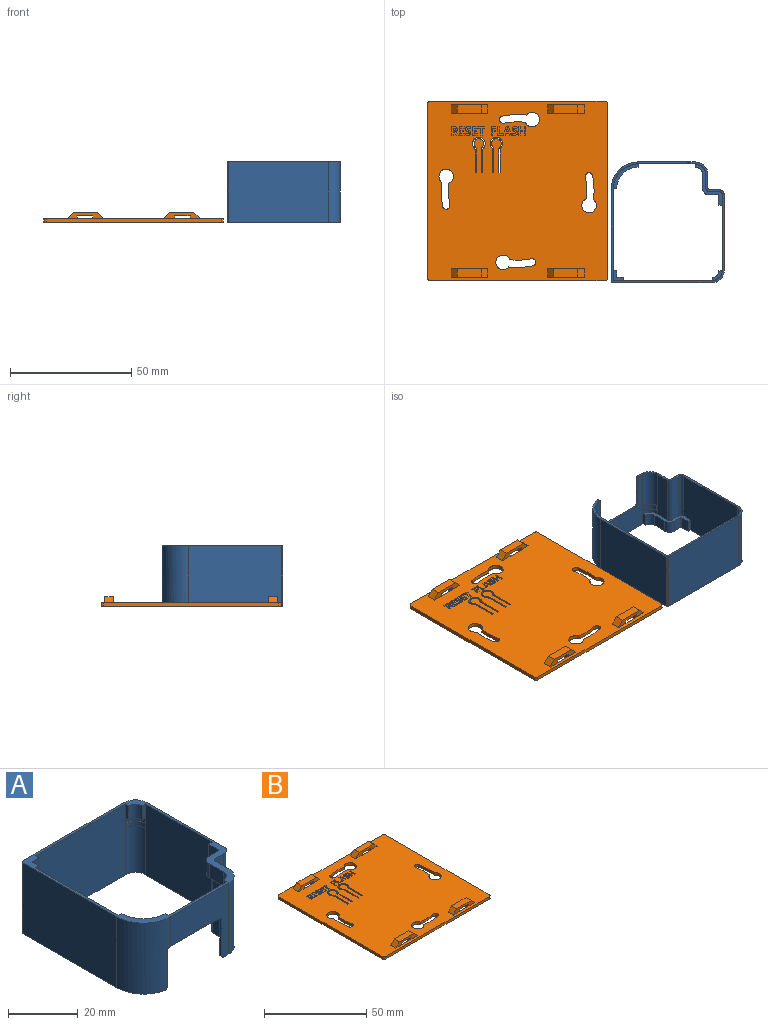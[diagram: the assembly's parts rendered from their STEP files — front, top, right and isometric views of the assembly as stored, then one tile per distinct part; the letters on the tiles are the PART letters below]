
ASSEMBLY  parts=2 mates=1
PART A: 74 faces, bbox 46.5x49.8x25 mm
  f0: plane 49.75x46.5mm, normal (0,0,1), area 215.3mm2, adj f38,f39,f40,f41,f42,f43,f44,f45
  f1: plane 2.42x0.2mm, normal (0,1,0), area 0.5mm2, adj f2,f3,f4,f11
  f2: cone r=2.6mm half-angle=60deg, axis (0,0,-1), area 1.5mm2, adj f1,f3,f19,f20
  f3: cylinder r=4mm len=4mm, axis (0,0,1), area 14.5mm2, adj f1,f2,f4,f20
  f4: plane 4.2x4.2mm, normal (0,0,1), area 1.3mm2, adj f1,f3,f20,f21
  f5: cone r=8.6mm half-angle=60deg, axis (0,0,-1), area 3.7mm2, adj f6,f22,f27,f28
  f6: cylinder r=10mm len=10mm, axis (0,0,1), area 36.3mm2, adj f5,f7,f22,f28
  f7: plane 10.2x10.2mm, normal (0,0,1), area 3.2mm2, adj f6,f22,f28,f29
  f8: cylinder r=4mm len=4mm, axis (0,0,1), area 9.3mm2, adj f9,f10,f18,f30
  f9: cone r=3.2mm half-angle=30deg, axis (0,0,-1), area 2.6mm2, adj f8,f18,f30,f31
  f10: plane 4.2x4.2mm, normal (0,0,1), area 1.3mm2, adj f8,f18,f30,f33
  f11: plane 20x5.8mm, normal (-1,0,0), area 116mm2, adj f1,f12,f19,f21,f37,f61
  f12: cylinder r=1.3mm len=20mm, axis (0,0,1), area 40.8mm2, adj f11,f13,f37,f61
  f13: plane 20x3.75mm, normal (0,1,0), area 75mm2, adj f12,f17,f37,f61
  f14: cylinder r=1mm len=1mm, axis (0,1,0), area 1.3mm2, adj f15,f23,f27,f73
  f15: plane 12.5x0.81mm, normal (1,0,0), area 10.1mm2, adj f14,f16,f27,f73
  f16: cylinder r=1mm len=1mm, axis (0,-1,0), area 1.3mm2, adj f15,f27,f61,f73
  f17: cylinder r=1.7mm len=20mm, axis (0,0,1), area 53.4mm2, adj f13,f37,f60,f61
  f18: plane 1.83x0.2mm, normal (0,-1,0), area 0.3mm2, adj f8,f9,f10,f60
  f19: cylinder r=4.2mm len=15.78mm, axis (0,0,1), area 104.1mm2, adj f2,f11,f52,f61
  f20: plane 2.42x0.2mm, normal (-1,0,0), area 0.5mm2, adj f2,f3,f4,f52
  f21: cylinder r=4.2mm len=4.2mm, axis (0,0,1), area 11.9mm2, adj f4,f11,f37,f52
  f22: plane 2.42x0.2mm, normal (1,0,0), area 0.5mm2, adj f5,f6,f7,f52
  f23: plane 20x0.8mm, normal (0,0,-1), area 16mm2, adj f14,f24,f27,f52,f72,f73
  f24: cylinder r=1mm len=1mm, axis (0,-1,0), area 1.3mm2, adj f23,f25,f52,f72
  f25: plane 12.5x0.8mm, normal (-1,0,0), area 10mm2, adj f24,f26,f52,f72
  f26: cylinder r=1mm len=1mm, axis (0,1,0), area 1.3mm2, adj f25,f52,f61,f72
  f27: cylinder r=10.2mm len=15.78mm, axis (0,0,1), area 234.6mm2, adj f5,f14,f15,f16,f23,f49,f52,f61
  f28: plane 2.42x0.2mm, normal (0,1,0), area 0.5mm2, adj f5,f6,f7,f49
  f29: cylinder r=10.2mm len=10.2mm, axis (0,0,1), area 28.8mm2, adj f7,f34,f49,f52
  f30: plane 1.83x0.2mm, normal (-1,0,0), area 0.3mm2, adj f8,f9,f10,f45
  f31: cylinder r=4.2mm len=16.37mm, axis (0,0,1), area 108mm2, adj f9,f45,f60,f61
  f32: cylinder r=0.5mm len=20mm, axis (0,0,1), area 15.7mm2, adj f36,f45,f49,f61
  f33: cylinder r=4.2mm len=4.2mm, axis (0,0,1), area 11.9mm2, adj f10,f35,f45,f60
  f34: plane 10.2x10.2mm, normal (0,0,-1), area 20.9mm2, adj f29,f39,f50,f51
  f35: plane 4.2x4.2mm, normal (0,0,-1), area 7.7mm2, adj f33,f42,f43,f44
  f36: plane 4.2x4.2mm, normal (0,0,-1), area 9.8mm2, adj f32,f40,f41,f45,f46,f47,f48,f49
  f37: plane 17x10.95mm, normal (0,0,-1), area 33.3mm2, adj f11,f12,f13,f17,f21,f38,f53,f54
  f38: plane 5x1.4mm, normal (-1,0,0), area 7mm2, adj f0,f37,f52,f53
  f39: plane 5x1.4mm, normal (0,1,0), area 7mm2, adj f0,f34,f49,f51
  f40: cylinder r=0.5mm len=5mm, axis (0,0,1), area 3.9mm2, adj f0,f36,f46,f48
  f41: plane 5x1.4mm, normal (1,0,0), area 7mm2, adj f0,f36,f45,f46
  f42: plane 5x1.4mm, normal (0,-1,0), area 7mm2, adj f0,f35,f44,f60
  f43: plane 5x1.4mm, normal (-1,0,0), area 7mm2, adj f0,f35,f44,f45
  f44: cylinder r=2.8mm len=5mm, axis (0,0,1), area 22mm2, adj f0,f35,f42,f43
  f45: plane 40.2x25mm, normal (0,-1,0), area 986.5mm2, adj f0,f30,f31,f32,f33,f36,f41,f43
  f46: plane 5x2.3mm, normal (0,-1,0), area 11.5mm2, adj f0,f36,f40,f41
  f47: plane 5x1.4mm, normal (0,-1,0), area 7mm2, adj f0,f36,f48,f49
  f48: plane 5x2.3mm, normal (1,0,0), area 11.5mm2, adj f0,f36,f40,f47
  f49: plane 37.45x25mm, normal (1,0,0), area 917.8mm2, adj f0,f27,f28,f29,f32,f36,f39,f47
  f50: plane 5x1.4mm, normal (1,0,0), area 7mm2, adj f0,f34,f51,f52
  f51: cylinder r=8.8mm len=8.8mm, axis (0,0,1), area 69.1mm2, adj f0,f34,f39,f50
  f52: plane 25x23.75mm, normal (0,1,0), area 292.9mm2, adj f0,f19,f20,f21,f22,f23,f24,f25
  f53: cylinder r=2.8mm len=5mm, axis (0,0,1), area 22mm2, adj f0,f37,f38,f54
  f54: plane 5.8x5mm, normal (-1,0,0), area 29mm2, adj f0,f37,f53,f55
  f55: cylinder r=2.7mm len=5mm, axis (0,0,1), area 21.2mm2, adj f0,f37,f54,f56
  f56: plane 5x3.75mm, normal (0,1,0), area 18.8mm2, adj f0,f37,f55,f59
  f57: plane 5x1.4mm, normal (0,1,0), area 7mm2, adj f0,f37,f58,f60
  f58: plane 5x4mm, normal (-1,0,0), area 20mm2, adj f0,f37,f57,f59
  f59: cylinder r=0.3mm len=5mm, axis (0,0,1), area 2.4mm2, adj f0,f37,f56,f58
  f60: plane 30.95x25mm, normal (-1,0,0), area 753.7mm2, adj f0,f17,f18,f31,f33,f37,f42,f57
  f61: plane 49.75x46.5mm, normal (0,0,-1), area 124.4mm2, adj f11,f12,f13,f16,f17,f19,f26,f27
  f62: cylinder r=5mm len=25mm, axis (0,0,1), area 196.3mm2, adj f0,f61,f64,f72
  f63: cylinder r=0.5mm len=25mm, axis (0,0,-1), area 19.6mm2, adj f0,f61,f64,f65
  f64: plane 25x5.8mm, normal (1,0,0), area 145mm2, adj f0,f61,f62,f63
  f65: plane 25x3.75mm, normal (0,-1,0), area 93.8mm2, adj f0,f61,f63,f66
  f66: cylinder r=2.5mm len=25mm, axis (0,0,1), area 98.2mm2, adj f0,f61,f65,f67
  f67: plane 30.95x25mm, normal (1,0,0), area 773.8mm2, adj f0,f61,f66,f68
  f68: cylinder r=5mm len=25mm, axis (0,0,1), area 196.3mm2, adj f0,f61,f67,f70
  f69: cylinder r=0.5mm len=25mm, axis (0,0,-1), area 19.6mm2, adj f0,f61,f70,f71
  f70: plane 41x25mm, normal (0,1,0), area 1025mm2, adj f0,f61,f68,f69
  f71: plane 38.25x25mm, normal (-1,0,0), area 956.3mm2, adj f0,f61,f69,f73
  f72: plane 25x23.75mm, normal (0,-1,0), area 292.9mm2, adj f0,f23,f24,f25,f26,f61,f62,f73
  f73: cylinder r=11mm len=25mm, axis (0,0,1), area 413.8mm2, adj f0,f14,f15,f16,f23,f61,f71,f72
PART B: 291 faces, bbox 74x74x4 mm
  f0: plane 74x74mm, normal (0,0,1), area 4941.7mm2, adj f2,f3,f4,f5,f6,f7,f8,f9
  f1: plane 47.35x44.1mm, normal (0,0,-1), area 1874.9mm2, adj f73,f74,f75,f76,f77,f78,f79,f80
  f2: plane 15x2.5mm, normal (0,-1,0), area 23.6mm2, adj f0,f34,f35,f36,f37,f55,f56,f65
  f3: plane 15x2.5mm, normal (0,-1,0), area 23.6mm2, adj f0,f4,f33,f38,f39,f50,f54,f66
  f4: plane 3.5x1.2mm, normal (-1,0,0), area 3.9mm2, adj f0,f3,f32,f39,f53,f54
  f5: plane 15x2.5mm, normal (0,1,0), area 23.6mm2, adj f0,f28,f43,f44,f45,f67,f72
  f6: plane 15x2.5mm, normal (0,1,0), area 23.6mm2, adj f0,f34,f35,f36,f37,f65,f69
  f7: plane 72x1.5mm, normal (1,0,0), area 108mm2, adj f0,f46,f49,f64
  f8: plane 72x1.5mm, normal (0,1,0), area 108mm2, adj f0,f46,f47,f64
  f9: plane 72x1.5mm, normal (-1,0,0), area 108mm2, adj f0,f47,f48,f64
  f10: plane 72x1.5mm, normal (0,-1,0), area 108mm2, adj f0,f48,f49,f64
  f11: cylinder r=28.5mm len=8.9mm, axis (0,0,-1), area 13.4mm2, adj f0,f12,f14,f64
  f12: cylinder r=3mm len=6mm, axis (0,0,-1), area 23.6mm2, adj f0,f11,f13,f64
  f13: cylinder r=31.5mm len=9.97mm, axis (0,0,-1), area 15mm2, adj f0,f12,f14,f64
  f14: cylinder r=1.5mm len=2.97mm, axis (0,0,-1), area 7.1mm2, adj f0,f11,f13,f64
  f15: cylinder r=3mm len=6mm, axis (0,0,-1), area 23.6mm2, adj f0,f16,f18,f64
  f16: cylinder r=31.5mm len=9.97mm, axis (0,0,-1), area 15mm2, adj f0,f15,f17,f64
  f17: cylinder r=1.5mm len=2.97mm, axis (0,0,-1), area 7.1mm2, adj f0,f16,f18,f64
  f18: cylinder r=28.5mm len=8.9mm, axis (0,0,-1), area 13.4mm2, adj f0,f15,f17,f64
  f19: cylinder r=3mm len=6mm, axis (0,0,-1), area 23.6mm2, adj f0,f20,f22,f64
  f20: cylinder r=31.5mm len=9.97mm, axis (0,0,-1), area 15mm2, adj f0,f19,f21,f64
  f21: cylinder r=1.5mm len=2.97mm, axis (0,0,-1), area 7.1mm2, adj f0,f20,f22,f64
  f22: cylinder r=28.5mm len=8.9mm, axis (0,0,-1), area 13.4mm2, adj f0,f19,f21,f64
  f23: cylinder r=31.5mm len=9.97mm, axis (0,0,-1), area 15mm2, adj f0,f24,f26,f64
  f24: cylinder r=1.5mm len=2.97mm, axis (0,0,-1), area 7.1mm2, adj f0,f23,f25,f64
  f25: cylinder r=28.5mm len=8.9mm, axis (0,0,-1), area 13.4mm2, adj f0,f24,f26,f64
  f26: cylinder r=3mm len=6mm, axis (0,0,-1), area 23.6mm2, adj f0,f23,f25,f64
  f27: plane 15x2.5mm, normal (0,-1,0), area 23.6mm2, adj f0,f28,f43,f44,f45,f67,f72
  f28: plane 10x3.5mm, normal (0,0,1), area 35mm2, adj f5,f27,f67,f72
  f29: plane 15x2.5mm, normal (0,1,0), area 23.6mm2, adj f0,f31,f40,f41,f42,f68,f71
  f30: plane 15x2.5mm, normal (0,-1,0), area 23.6mm2, adj f0,f31,f40,f41,f42,f68,f71
  f31: plane 10x3.5mm, normal (0,0,1), area 35mm2, adj f29,f30,f68,f71
  f32: plane 15x2.5mm, normal (0,1,0), area 23.6mm2, adj f0,f4,f33,f38,f39,f66,f70
  f33: plane 10x3.5mm, normal (0,0,1), area 35mm2, adj f3,f32,f66,f70
  f34: plane 10x3.5mm, normal (0,0,1), area 35mm2, adj f2,f6,f65,f69
  f35: plane 6.4x3.5mm, normal (0,0,-1), area 22.4mm2, adj f2,f6,f36,f37
  f36: plane 3.5x1.2mm, normal (-1,0,0), area 3.9mm2, adj f0,f2,f6,f35,f56,f59
  f37: plane 3.5x1.2mm, normal (1,0,0), area 4.2mm2, adj f0,f2,f6,f35
  f38: plane 3.5x1.2mm, normal (1,0,0), area 4.2mm2, adj f0,f3,f32,f39
  f39: plane 6.4x3.5mm, normal (0,0,-1), area 22.4mm2, adj f3,f4,f32,f38
  f40: plane 3.5x2.7mm, normal (-1,0,0), area 9.4mm2, adj f29,f30,f41,f62,f63,f64
  f41: plane 6.4x3.5mm, normal (0,0,-1), area 22.4mm2, adj f29,f30,f40,f42
  f42: plane 3.5x2.7mm, normal (1,0,0), area 9.4mm2, adj f29,f30,f41,f62,f63,f64
  f43: plane 3.5x2.7mm, normal (1,0,0), area 9.4mm2, adj f5,f27,f45,f60,f61,f64
  f44: plane 3.5x2.7mm, normal (-1,0,0), area 9.4mm2, adj f5,f27,f45,f60,f61,f64
  f45: plane 6.4x3.5mm, normal (0,0,-1), area 22.4mm2, adj f5,f27,f43,f44
  f46: cylinder r=1mm len=1.5mm, axis (0,0,1), area 2.4mm2, adj f0,f7,f8,f64
  f47: cylinder r=1mm len=1.5mm, axis (0,0,-1), area 2.4mm2, adj f0,f8,f9,f64
  f48: cylinder r=1mm len=1.5mm, axis (0,0,1), area 2.4mm2, adj f0,f9,f10,f64
  f49: cylinder r=1mm len=1.5mm, axis (0,0,-1), area 2.4mm2, adj f0,f7,f10,f64
  f50: plane 3.5x1.6mm, normal (-1,0,0), area 5.6mm2, adj f0,f3,f51,f53,f54,f64
  f51: plane 6.4x1.5mm, normal (0,1,0), area 9.6mm2, adj f0,f50,f52,f64
  f52: plane 3.5x1.5mm, normal (1,0,0), area 5.2mm2, adj f0,f51,f53,f64
  f53: plane 6.4x1.6mm, normal (0,-1,0), area 9.6mm2, adj f0,f4,f50,f52,f54,f64
  f54: plane 3.28x0.14mm, normal (0,0,-1), area 0.4mm2, adj f3,f4,f50,f53
  f55: plane 3.5x1.6mm, normal (-1,0,0), area 5.6mm2, adj f0,f2,f56,f57,f59,f64
  f56: plane 3.44x0.14mm, normal (0,0,-1), area 0.5mm2, adj f2,f36,f55,f59
  f57: plane 6.4x1.5mm, normal (0,1,0), area 9.6mm2, adj f0,f55,f58,f64
  f58: plane 3.5x1.5mm, normal (1,0,0), area 5.2mm2, adj f0,f57,f59,f64
  f59: plane 6.4x1.6mm, normal (0,-1,0), area 9.6mm2, adj f0,f36,f55,f56,f58,f64
  f60: plane 6.4x1.5mm, normal (0,1,0), area 9.6mm2, adj f0,f43,f44,f64
  f61: plane 6.4x1.5mm, normal (0,-1,0), area 9.6mm2, adj f0,f43,f44,f64
  f62: plane 6.4x1.5mm, normal (0,-1,0), area 9.6mm2, adj f0,f40,f42,f64
  f63: plane 6.4x1.5mm, normal (0,1,0), area 9.6mm2, adj f0,f40,f42,f64
  f64: plane 74x74mm, normal (0,0,-1), area 2875.4mm2, adj f7,f8,f9,f10,f11,f12,f13,f14
  f65: plane 3.5x2.5mm, normal (-0.71,0,0.71), area 12.4mm2, adj f0,f2,f6,f34
  f66: plane 3.5x2.5mm, normal (-0.71,0,0.71), area 12.4mm2, adj f0,f3,f32,f33
  f67: plane 3.5x2.5mm, normal (-0.71,0,0.71), area 12.4mm2, adj f0,f5,f27,f28
  f68: plane 3.5x2.5mm, normal (-0.71,0,0.71), area 12.4mm2, adj f0,f29,f30,f31
  f69: plane 3.5x2.5mm, normal (0.71,0,0.71), area 12.4mm2, adj f0,f2,f6,f34
  f70: plane 3.5x2.5mm, normal (0.71,0,0.71), area 12.4mm2, adj f0,f3,f32,f33
  f71: plane 3.5x2.5mm, normal (0.71,0,0.71), area 12.4mm2, adj f0,f29,f30,f31
  f72: plane 3.5x2.5mm, normal (0.71,0,0.71), area 12.4mm2, adj f0,f5,f27,f28
  f73: plane 1.5x0.6mm, normal (0,1,0), area 0.9mm2, adj f0,f1,f79,f84
  f74: plane 1.5x0.6mm, normal (0,1,0), area 0.9mm2, adj f0,f1,f75,f80
  f75: plane 9.35x1.5mm, normal (1,0,0), area 14mm2, adj f0,f1,f74,f76
  f76: cylinder r=1.4mm len=1.5mm, axis (0,0,1), area 1.5mm2, adj f0,f1,f75,f77
  f77: cylinder r=2.6mm len=5.2mm, axis (0,0,1), area 17.9mm2, adj f0,f1,f76,f78
  f78: cylinder r=1.4mm len=1.5mm, axis (0,0,1), area 1.5mm2, adj f0,f1,f77,f79
  f79: plane 9.35x1.5mm, normal (-1,0,0), area 14mm2, adj f0,f1,f73,f78
  f80: plane 9.35x1.5mm, normal (-1,0,0), area 14mm2, adj f0,f1,f74,f81
  f81: cylinder r=2mm len=1.5mm, axis (0,0,1), area 2.2mm2, adj f0,f1,f80,f82
  f82: cylinder r=2mm len=4mm, axis (0,0,1), area 13.8mm2, adj f0,f1,f81,f83
  f83: cylinder r=2mm len=1.5mm, axis (0,0,1), area 2.2mm2, adj f0,f1,f82,f84
  f84: plane 9.35x1.5mm, normal (1,0,0), area 14mm2, adj f0,f1,f73,f83
  f85: plane 1.5x0.6mm, normal (0,1,0), area 0.9mm2, adj f0,f1,f91,f96
  f86: plane 1.5x0.6mm, normal (0,1,0), area 0.9mm2, adj f0,f1,f87,f92
  f87: plane 9.35x1.5mm, normal (1,0,0), area 14mm2, adj f0,f1,f86,f88
  f88: cylinder r=1.4mm len=1.5mm, axis (0,0,1), area 1.5mm2, adj f0,f1,f87,f89
  f89: cylinder r=2.6mm len=5.2mm, axis (0,0,1), area 17.9mm2, adj f0,f1,f88,f90
  f90: cylinder r=1.4mm len=1.5mm, axis (0,0,1), area 1.5mm2, adj f0,f1,f89,f91
  f91: plane 9.35x1.5mm, normal (-1,0,0), area 14mm2, adj f0,f1,f85,f90
  f92: plane 9.35x1.5mm, normal (-1,0,0), area 14mm2, adj f0,f1,f86,f93
  f93: cylinder r=2mm len=1.5mm, axis (0,0,1), area 2.2mm2, adj f0,f1,f92,f94
  f94: cylinder r=2mm len=4mm, axis (0,0,1), area 13.8mm2, adj f0,f1,f93,f95
  f95: cylinder r=2mm len=1.5mm, axis (0,0,1), area 2.2mm2, adj f0,f1,f94,f96
  f96: plane 9.35x1.5mm, normal (1,0,0), area 14mm2, adj f0,f1,f85,f95
  f97: plane 1.43x0.8mm, normal (1,0,0), area 1.1mm2, adj f1,f111,f112,f131
  f98: plane 1.41x0.8mm, normal (0,-1,0), area 1.1mm2, adj f1,f108,f110,f131
  f99: cylinder r=0.1mm len=0.8mm, axis (0,0,1), area 0.1mm2, adj f1,f105,f107,f131
  f100: plane 1.4x0.8mm, normal (-1,0,0), area 1.1mm2, adj f1,f104,f105,f131
  f101: plane 1.43x0.8mm, normal (0,1,0), area 1.1mm2, adj f1,f103,f118,f131
  f102: plane 1.43x0.8mm, normal (1,0,0), area 1.1mm2, adj f1,f103,f104,f131
  f103: cylinder r=2.4mm len=2.8mm, axis (0,0,1), area 3.7mm2, adj f1,f101,f102,f131
  f104: plane 35.7x0.8mm, normal (0,1,0), area 28.6mm2, adj f1,f100,f102,f131
  f105: plane 2.7x0.8mm, normal (0,1,0), area 2.2mm2, adj f1,f99,f100,f131
  f106: plane 1.4x0.8mm, normal (0,1,0), area 1.1mm2, adj f1,f107,f108,f131
  f107: plane 2.7x0.8mm, normal (-1,0,0), area 2.2mm2, adj f1,f99,f106,f131
  f108: plane 32.95x0.8mm, normal (-1,0,0), area 26.4mm2, adj f1,f98,f106,f131
  f109: plane 1.41x0.8mm, normal (-1,0,0), area 1.1mm2, adj f1,f110,f111,f131
  f110: cylinder r=8.4mm len=8.8mm, axis (0,0,1), area 11.2mm2, adj f1,f98,f109,f131
  f111: plane 22.95x0.8mm, normal (0,-1,0), area 18.4mm2, adj f1,f97,f109,f131
  f112: cylinder r=2.4mm len=2.8mm, axis (0,0,1), area 3.3mm2, adj f1,f97,f113,f131
  f113: plane 5.8x0.8mm, normal (1,0,0), area 4.6mm2, adj f1,f112,f114,f131
  f114: cylinder r=3.1mm len=3.1mm, axis (0,0,1), area 3.9mm2, adj f1,f113,f115,f131
  f115: plane 3.65x0.8mm, normal (0,-1,0), area 2.9mm2, adj f1,f114,f117,f131
  f116: plane 1.4x0.8mm, normal (0,-1,0), area 1.1mm2, adj f1,f117,f118,f131
  f117: plane 4.3x0.8mm, normal (1,0,0), area 3.4mm2, adj f1,f115,f116,f131
  f118: plane 26.15x0.8mm, normal (1,0,0), area 20.9mm2, adj f1,f101,f116,f131
  f119: cylinder r=5.4mm len=5.4mm, axis (0,0,1), area 6.8mm2, adj f64,f121,f129,f131
  f120: cylinder r=0.1mm len=0.8mm, axis (0,0,-1), area 0.1mm2, adj f64,f121,f122,f131
  f121: plane 5.8x0.8mm, normal (-1,0,0), area 4.6mm2, adj f64,f119,f120,f131
  f122: plane 3.75x0.8mm, normal (0,1,0), area 3mm2, adj f64,f120,f123,f131
  f123: cylinder r=2.9mm len=2.9mm, axis (0,0,1), area 3.6mm2, adj f64,f122,f124,f131
  f124: plane 30.95x0.8mm, normal (-1,0,0), area 24.8mm2, adj f64,f123,f125,f131
  f125: cylinder r=5.4mm len=5.4mm, axis (0,0,1), area 6.8mm2, adj f64,f124,f127,f131
  f126: cylinder r=0.9mm len=0.9mm, axis (0,0,-1), area 1.1mm2, adj f64,f127,f128,f131
  f127: plane 41x0.8mm, normal (0,-1,0), area 32.8mm2, adj f64,f125,f126,f131
  f128: plane 38.25x0.8mm, normal (1,0,0), area 30.6mm2, adj f64,f126,f130,f131
  f129: plane 23.75x0.8mm, normal (0,1,0), area 19mm2, adj f64,f119,f130,f131
  f130: cylinder r=11.4mm len=11.4mm, axis (0,0,1), area 14.3mm2, adj f64,f128,f129,f131
  f131: plane 50.55x47.3mm, normal (0,0,-1), area 359.4mm2, adj f97,f98,f99,f100,f101,f102,f103,f104
  f132: plane 2x0.4mm, normal (0,1,0), area 0.8mm2, adj f0,f133,f143,f144
  f133: plane 0.61x0.4mm, normal (-1,0,0), area 0.2mm2, adj f0,f132,f134,f144
  f134: plane 1.26x0.4mm, normal (0,-1,0), area 0.5mm2, adj f0,f133,f135,f144
  f135: plane 0.89x0.4mm, normal (-1,0,0), area 0.4mm2, adj f0,f134,f136,f144
  f136: plane 1.18x0.4mm, normal (0,1,0), area 0.5mm2, adj f0,f135,f137,f144
  f137: plane 0.6x0.4mm, normal (-1,0,0), area 0.2mm2, adj f0,f136,f138,f144
  f138: plane 1.18x0.4mm, normal (0,-1,0), area 0.5mm2, adj f0,f137,f139,f144
  f139: plane 0.76x0.4mm, normal (-1,0,0), area 0.3mm2, adj f0,f138,f140,f144
  f140: plane 1.26x0.4mm, normal (0,1,0), area 0.5mm2, adj f0,f139,f141,f144
  f141: plane 0.6x0.4mm, normal (-1,0,0), area 0.2mm2, adj f0,f140,f142,f144
  f142: plane 2x0.4mm, normal (0,-1,0), area 0.8mm2, adj f0,f141,f143,f144
  f143: plane 3.47x0.4mm, normal (1,0,0), area 1.4mm2, adj f0,f132,f142,f144
  f144: plane 3.47x2mm, normal (0,0,1), area 4.8mm2, adj f132,f133,f134,f135,f136,f137,f138,f139
  f145: extruded ~1.27x0.4mm, area 0.5mm2, adj f146,f156,f157,f290
  f146: plane 0.9x0.4mm, normal (0,-1,0), area 0.4mm2, adj f145,f147,f157,f290
  f147: extruded ~1.5x0.45mm, area 0.6mm2, adj f146,f156,f157,f290
  f148: plane 0.83x0.4mm, normal (0.96,0.29,0), area 0.3mm2, adj f0,f149,f155,f157
  f149: plane 0.79x0.4mm, normal (0,1,0), area 0.3mm2, adj f0,f148,f150,f157
  f150: plane 3.49x1.23mm, normal (-0.94,-0.33,0), area 1.5mm2, adj f0,f149,f151,f157
  f151: plane 0.9x0.4mm, normal (0,-1,0), area 0.4mm2, adj f0,f150,f152,f157
  f152: plane 3.49x1.23mm, normal (0.94,-0.33,0), area 1.5mm2, adj f0,f151,f153,f157
  f153: plane 0.79x0.4mm, normal (0,1,0), area 0.3mm2, adj f0,f152,f154,f157
  f154: plane 0.83x0.4mm, normal (-0.96,0.29,0), area 0.3mm2, adj f0,f153,f155,f157
  f155: plane 1.27x0.4mm, normal (0,1,0), area 0.5mm2, adj f0,f148,f154,f157
  f156: extruded ~0.4x0.23mm, area 0.1mm2, adj f145,f147,f157,f290
  f157: plane 3.49x3.35mm, normal (0,0,1), area 5.5mm2, adj f145,f146,f147,f148,f149,f150,f151,f152
  f158: extruded ~0.74x0.4mm, area 0.3mm2, adj f0,f159,f185,f186
  f159: extruded ~0.57x0.4mm, area 0.2mm2, adj f0,f158,f160,f186
  f160: extruded ~0.67x0.47mm, area 0.3mm2, adj f0,f159,f161,f186
  f161: extruded ~0.47x0.4mm, area 0.2mm2, adj f0,f160,f162,f186
  f162: extruded ~0.4x0.14mm, area 0.1mm2, adj f0,f161,f163,f186
  f163: extruded ~0.4x0.17mm, area 0.1mm2, adj f0,f162,f164,f186
  f164: extruded ~0.4x0.25mm, area 0.1mm2, adj f0,f163,f165,f186
  f165: extruded ~0.4x0.32mm, area 0.1mm2, adj f0,f164,f166,f186
  f166: extruded ~0.4x0.36mm, area 0.1mm2, adj f0,f165,f167,f186
  f167: extruded ~0.46x0.4mm, area 0.2mm2, adj f0,f166,f168,f186
  f168: plane 0.57x0.4mm, normal (-0.92,0.38,0), area 0.2mm2, adj f0,f167,f169,f186
  f169: extruded ~0.51x0.4mm, area 0.2mm2, adj f0,f168,f170,f186
  f170: extruded ~0.52x0.4mm, area 0.2mm2, adj f0,f169,f171,f186
  f171: extruded ~0.86x0.4mm, area 0.4mm2, adj f0,f170,f172,f186
  f172: extruded ~0.72x0.4mm, area 0.3mm2, adj f0,f171,f173,f186
  f173: extruded ~0.43x0.4mm, area 0.2mm2, adj f0,f172,f174,f186
  f174: extruded ~0.4x0.32mm, area 0.2mm2, adj f0,f173,f175,f186
  f175: extruded ~0.48x0.4mm, area 0.2mm2, adj f0,f174,f176,f186
  f176: extruded ~0.45x0.4mm, area 0.2mm2, adj f0,f175,f177,f186
  f177: extruded ~0.4x0.17mm, area 0.1mm2, adj f0,f176,f178,f186
  f178: extruded ~0.4x0.18mm, area 0.1mm2, adj f0,f177,f179,f186
  f179: extruded ~0.4x0.28mm, area 0.1mm2, adj f0,f178,f180,f186
  f180: extruded ~0.4x0.37mm, area 0.2mm2, adj f0,f179,f181,f186
  f181: extruded ~0.45x0.4mm, area 0.2mm2, adj f0,f180,f182,f186
  f182: extruded ~0.59x0.4mm, area 0.3mm2, adj f0,f181,f183,f186
  f183: plane 0.68x0.4mm, normal (1,0,0), area 0.3mm2, adj f0,f182,f184,f186
  f184: extruded ~0.98x0.4mm, area 0.4mm2, adj f0,f183,f185,f186
  f185: extruded ~0.94x0.4mm, area 0.4mm2, adj f0,f158,f184,f186
  f186: plane 3.57x2.26mm, normal (0,0,1), area 4.5mm2, adj f158,f159,f160,f161,f162,f163,f164,f165
  f187: plane 2x0.4mm, normal (0,1,0), area 0.8mm2, adj f0,f188,f198,f199
  f188: plane 0.61x0.4mm, normal (-1,0,0), area 0.2mm2, adj f0,f187,f189,f199
  f189: plane 1.26x0.4mm, normal (0,-1,0), area 0.5mm2, adj f0,f188,f190,f199
  f190: plane 0.89x0.4mm, normal (-1,0,0), area 0.4mm2, adj f0,f189,f191,f199
  f191: plane 1.18x0.4mm, normal (0,1,0), area 0.5mm2, adj f0,f190,f192,f199
  f192: plane 0.6x0.4mm, normal (-1,0,0), area 0.2mm2, adj f0,f191,f193,f199
  f193: plane 1.18x0.4mm, normal (0,-1,0), area 0.5mm2, adj f0,f192,f194,f199
  f194: plane 0.76x0.4mm, normal (-1,0,0), area 0.3mm2, adj f0,f193,f195,f199
  f195: plane 1.26x0.4mm, normal (0,1,0), area 0.5mm2, adj f0,f194,f196,f199
  f196: plane 0.6x0.4mm, normal (-1,0,0), area 0.2mm2, adj f0,f195,f197,f199
  f197: plane 2x0.4mm, normal (0,-1,0), area 0.8mm2, adj f0,f196,f198,f199
  f198: plane 3.47x0.4mm, normal (1,0,0), area 1.4mm2, adj f0,f187,f197,f199
  f199: plane 3.47x2mm, normal (0,0,1), area 4.8mm2, adj f187,f188,f189,f190,f191,f192,f193,f194
  f200: plane 0.74x0.4mm, normal (0,1,0), area 0.3mm2, adj f0,f201,f207,f208
  f201: plane 2.86x0.4mm, normal (-1,0,0), area 1.1mm2, adj f0,f200,f202,f208
  f202: plane 0.94x0.4mm, normal (0,1,0), area 0.4mm2, adj f0,f201,f203,f208
  f203: plane 0.61x0.4mm, normal (-1,0,0), area 0.2mm2, adj f0,f202,f204,f208
  f204: plane 2.62x0.4mm, normal (0,-1,0), area 1mm2, adj f0,f203,f205,f208
  f205: plane 0.61x0.4mm, normal (1,0,0), area 0.2mm2, adj f0,f204,f206,f208
  f206: plane 0.94x0.4mm, normal (0,1,0), area 0.4mm2, adj f0,f205,f207,f208
  f207: plane 2.86x0.4mm, normal (1,0,0), area 1.1mm2, adj f0,f200,f206,f208
  f208: plane 3.47x2.62mm, normal (0,0,1), area 3.7mm2, adj f200,f201,f202,f203,f204,f205,f206,f207
  f209: plane 0.72x0.4mm, normal (0,1,0), area 0.3mm2, adj f0,f210,f218,f219
  f210: plane 1.37x0.4mm, normal (-1,0,0), area 0.5mm2, adj f0,f209,f211,f219
  f211: plane 1.18x0.4mm, normal (0,1,0), area 0.5mm2, adj f0,f210,f212,f219
  f212: plane 0.6x0.4mm, normal (-1,0,0), area 0.2mm2, adj f0,f211,f213,f219
  f213: plane 1.18x0.4mm, normal (0,-1,0), area 0.5mm2, adj f0,f212,f214,f219
  f214: plane 0.89x0.4mm, normal (-1,0,0), area 0.4mm2, adj f0,f213,f215,f219
  f215: plane 1.27x0.4mm, normal (0,1,0), area 0.5mm2, adj f0,f214,f216,f219
  f216: plane 0.6x0.4mm, normal (-1,0,0), area 0.2mm2, adj f0,f215,f217,f219
  f217: plane 1.99x0.4mm, normal (0,-1,0), area 0.8mm2, adj f0,f216,f218,f219
  f218: plane 3.47x0.4mm, normal (1,0,0), area 1.4mm2, adj f0,f209,f217,f219
  f219: plane 3.47x1.99mm, normal (0,0,1), area 4mm2, adj f209,f210,f211,f212,f213,f214,f215,f216
  f220: plane 1.33x0.4mm, normal (-1,0,0), area 0.5mm2, adj f0,f221,f238,f239
  f221: plane 0.4x0.39mm, normal (0,1,0), area 0.2mm2, adj f0,f220,f222,f239
  f222: plane 1.33x0.83mm, normal (0.85,0.53,0), area 0.6mm2, adj f0,f221,f223,f239
  f223: plane 0.82x0.4mm, normal (0,1,0), area 0.3mm2, adj f0,f222,f224,f239
  f224: extruded ~1.51x1.02mm, area 0.7mm2, adj f0,f223,f225,f239
  f225: extruded ~0.48x0.4mm, area 0.2mm2, adj f0,f224,f226,f239
  f226: extruded ~0.54x0.4mm, area 0.2mm2, adj f0,f225,f227,f239
  f227: extruded ~0.78x0.4mm, area 0.4mm2, adj f0,f226,f228,f239
  f228: extruded ~1.05x0.4mm, area 0.4mm2, adj f0,f227,f229,f239
  f229: plane 1.01x0.4mm, normal (0,-1,0), area 0.4mm2, adj f0,f228,f230,f239
  f230: plane 3.47x0.4mm, normal (1,0,0), area 1.4mm2, adj f0,f229,f238,f239
  f231: plane 0.4x0.24mm, normal (0,-1,0), area 0.1mm2, adj f232,f237,f239,f240
  f232: plane 0.94x0.4mm, normal (-1,0,0), area 0.4mm2, adj f231,f233,f239,f240
  f233: plane 0.4x0.22mm, normal (0,1,0), area 0.1mm2, adj f232,f234,f239,f240
  f234: extruded ~0.53x0.4mm, area 0.2mm2, adj f233,f235,f239,f240
  f235: extruded ~0.4x0.35mm, area 0.2mm2, adj f234,f236,f239,f240
  f236: extruded ~0.4x0.37mm, area 0.2mm2, adj f235,f237,f239,f240
  f237: extruded ~0.52x0.4mm, area 0.2mm2, adj f231,f236,f239,f240
  f238: plane 0.74x0.4mm, normal (0,1,0), area 0.3mm2, adj f0,f220,f230,f239
  f239: plane 3.47x2.77mm, normal (0,0,1), area 5.9mm2, adj f220,f221,f222,f223,f224,f225,f226,f227
  f240: plane 0.94x0.92mm, normal (0,0,1), area 0.8mm2, adj f231,f232,f233,f234,f235,f236,f237
  f241: plane 0.73x0.4mm, normal (0,1,0), area 0.3mm2, adj f0,f242,f252,f253
  f242: plane 3.47x0.4mm, normal (-1,0,0), area 1.4mm2, adj f0,f241,f243,f253
  f243: plane 0.73x0.4mm, normal (0,-1,0), area 0.3mm2, adj f0,f242,f244,f253
  f244: plane 1.36x0.4mm, normal (1,0,0), area 0.5mm2, adj f0,f243,f245,f253
  f245: plane 1.37x0.4mm, normal (0,-1,0), area 0.5mm2, adj f0,f244,f246,f253
  f246: plane 1.36x0.4mm, normal (-1,0,0), area 0.5mm2, adj f0,f245,f247,f253
  f247: plane 0.74x0.4mm, normal (0,-1,0), area 0.3mm2, adj f0,f246,f248,f253
  f248: plane 3.47x0.4mm, normal (1,0,0), area 1.4mm2, adj f0,f247,f249,f253
  f249: plane 0.74x0.4mm, normal (0,1,0), area 0.3mm2, adj f0,f248,f250,f253
  f250: plane 1.5x0.4mm, normal (-1,0,0), area 0.6mm2, adj f0,f249,f251,f253
  f251: plane 1.37x0.4mm, normal (0,1,0), area 0.5mm2, adj f0,f250,f252,f253
  f252: plane 1.5x0.4mm, normal (1,0,0), area 0.6mm2, adj f0,f241,f251,f253
  f253: plane 3.47x2.84mm, normal (0,0,1), area 5.9mm2, adj f241,f242,f243,f244,f245,f246,f247,f248
  f254: extruded ~0.74x0.4mm, area 0.3mm2, adj f0,f255,f281,f282
  f255: extruded ~0.57x0.4mm, area 0.2mm2, adj f0,f254,f256,f282
  f256: extruded ~0.67x0.47mm, area 0.3mm2, adj f0,f255,f257,f282
  f257: extruded ~0.47x0.4mm, area 0.2mm2, adj f0,f256,f258,f282
  f258: extruded ~0.4x0.14mm, area 0.1mm2, adj f0,f257,f259,f282
  f259: extruded ~0.4x0.17mm, area 0.1mm2, adj f0,f258,f260,f282
  f260: extruded ~0.4x0.25mm, area 0.1mm2, adj f0,f259,f261,f282
  f261: extruded ~0.4x0.32mm, area 0.1mm2, adj f0,f260,f262,f282
  f262: extruded ~0.4x0.36mm, area 0.1mm2, adj f0,f261,f263,f282
  f263: extruded ~0.46x0.4mm, area 0.2mm2, adj f0,f262,f264,f282
  f264: plane 0.57x0.4mm, normal (-0.92,0.38,0), area 0.2mm2, adj f0,f263,f265,f282
  f265: extruded ~0.51x0.4mm, area 0.2mm2, adj f0,f264,f266,f282
  f266: extruded ~0.52x0.4mm, area 0.2mm2, adj f0,f265,f267,f282
  f267: extruded ~0.86x0.4mm, area 0.4mm2, adj f0,f266,f268,f282
  f268: extruded ~0.72x0.4mm, area 0.3mm2, adj f0,f267,f269,f282
  f269: extruded ~0.43x0.4mm, area 0.2mm2, adj f0,f268,f270,f282
  f270: extruded ~0.4x0.32mm, area 0.2mm2, adj f0,f269,f271,f282
  f271: extruded ~0.48x0.4mm, area 0.2mm2, adj f0,f270,f272,f282
  f272: extruded ~0.45x0.4mm, area 0.2mm2, adj f0,f271,f273,f282
  f273: extruded ~0.4x0.17mm, area 0.1mm2, adj f0,f272,f274,f282
  f274: extruded ~0.4x0.18mm, area 0.1mm2, adj f0,f273,f275,f282
  f275: extruded ~0.4x0.28mm, area 0.1mm2, adj f0,f274,f276,f282
  f276: extruded ~0.4x0.37mm, area 0.2mm2, adj f0,f275,f277,f282
  f277: extruded ~0.45x0.4mm, area 0.2mm2, adj f0,f276,f278,f282
  f278: extruded ~0.59x0.4mm, area 0.3mm2, adj f0,f277,f279,f282
  f279: plane 0.68x0.4mm, normal (1,0,0), area 0.3mm2, adj f0,f278,f280,f282
  f280: extruded ~0.98x0.4mm, area 0.4mm2, adj f0,f279,f281,f282
  f281: extruded ~0.94x0.4mm, area 0.4mm2, adj f0,f254,f280,f282
  f282: plane 3.57x2.26mm, normal (0,0,1), area 4.5mm2, adj f254,f255,f256,f257,f258,f259,f260,f261
  f283: plane 3.47x0.4mm, normal (1,0,0), area 1.4mm2, adj f0,f284,f288,f289
  f284: plane 2.14x0.4mm, normal (0,1,0), area 0.9mm2, adj f0,f283,f285,f289
  f285: plane 0.61x0.4mm, normal (-1,0,0), area 0.2mm2, adj f0,f284,f286,f289
  f286: plane 1.41x0.4mm, normal (0,-1,0), area 0.6mm2, adj f0,f285,f287,f289
  f287: plane 2.86x0.4mm, normal (-1,0,0), area 1.1mm2, adj f0,f286,f288,f289
  f288: plane 0.74x0.4mm, normal (0,-1,0), area 0.3mm2, adj f0,f283,f287,f289
  f289: plane 3.47x2.14mm, normal (0,0,1), area 3.4mm2, adj f283,f284,f285,f286,f287,f288
  f290: plane 1.5x0.9mm, normal (0,0,1), area 0.7mm2, adj f145,f146,f147,f156
PLACE A rot(axis=(1,0,0),180deg) t=(61.61,-12.59,0)mm
PLACE B t=(-0.22,0.35,0)mm
MATE fastened A.f5 <-> B.f64  axis (0,0,-1) through (49.36,1.29,0)mm
